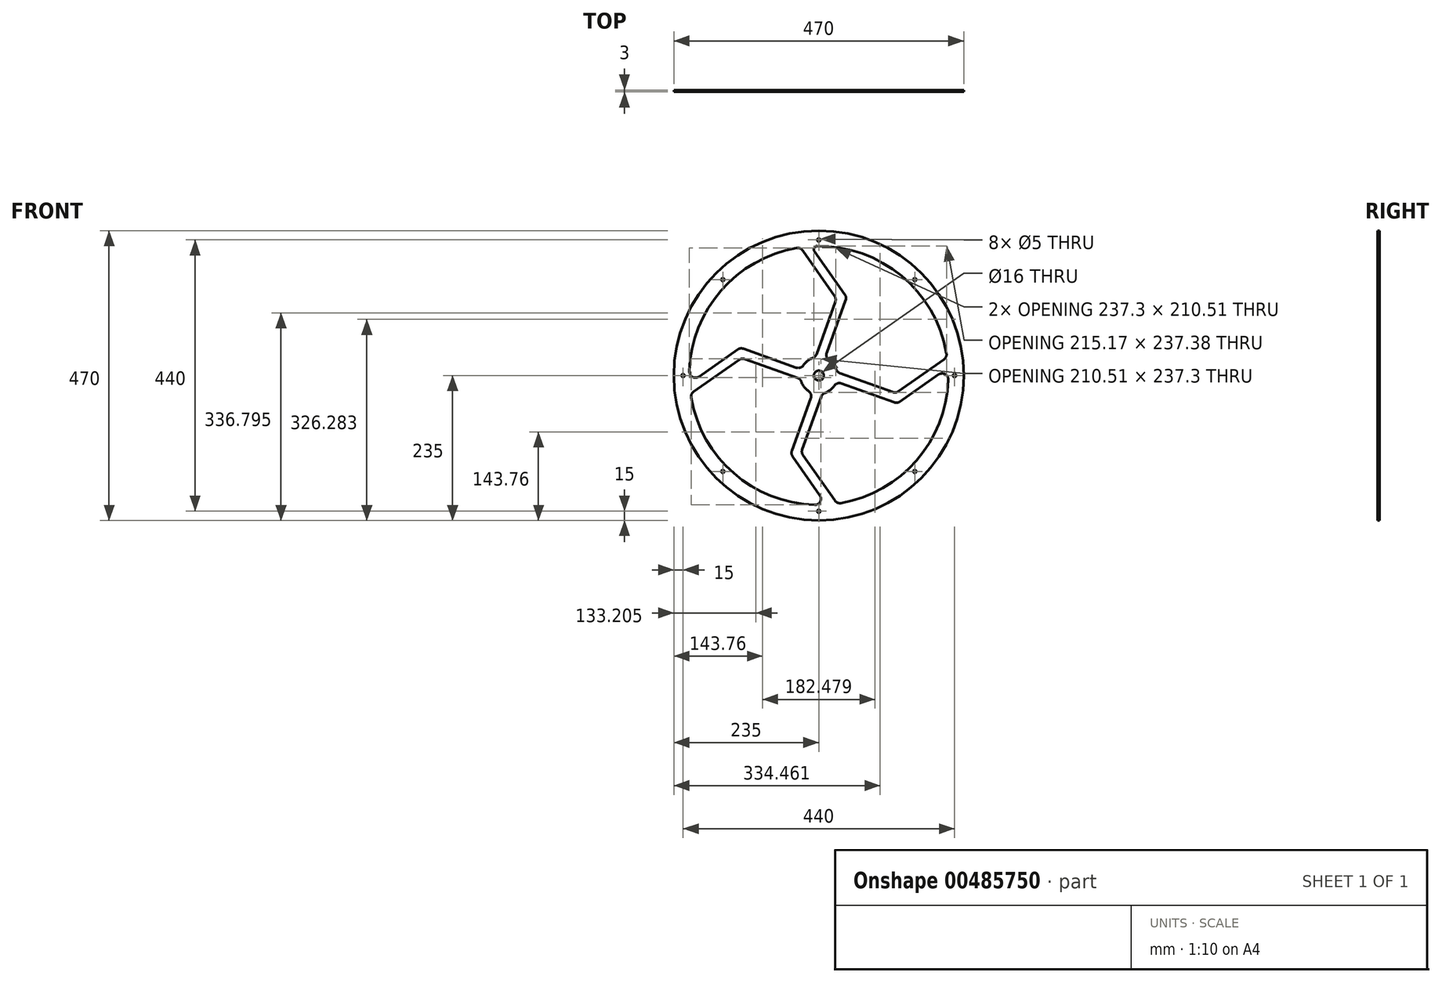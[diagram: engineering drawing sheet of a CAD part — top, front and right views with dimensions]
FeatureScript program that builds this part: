
annotation { "Feature Type Name" : "Feature", "Feature Type Description" : "" }
export const myFeature = defineFeature(function(context is Context, id is Id, definition is map)
    precondition{}
    {
        {
            var Q0;
            Q0=qCreatedBy(makeId("Front.planeOp"),FACE);
            var sketch = newSketch(context, id + "F0", { "sketchPlane" : qUnion([Q0]), "disableImprinting" : false});
            skCircle(sketch, "E0", {"center": v(0, 0) * mm, "radius": 235 * mm});
            skArc(sketch, "E1", {"start": v(206.9, 35.92) * mm, "mid": v(133.96, 161.72) * mm, "end": v(-3.21, 209.98) * mm});
            skArc(sketch, "E2", {"start": v(-9.97, 28.3) * mm, "mid": v(-18.38, 23.71) * mm, "end": v(-24.92, 16.7) * mm});
            skLineSegment(sketch, "E3", {"start": v(202.79, 26.02) * mm, "end": v(129.06, -25.6) * mm});
            skLineSegment(sketch, "E4", {"start": v(119.95, -26.82) * mm, "end": v(34.35, 3.87) * mm});
            skLineSegment(sketch, "E5", {"start": v(36.6, -12.87) * mm, "end": v(122.2, -43.56) * mm});
            skLineSegment(sketch, "E6", {"start": v(131.3, -42.34) * mm, "end": v(194.16, 1.67) * mm});
            skPoint(sketch, "E7.visualSharp", {"position": v(127.07, -45.31) * mm});
            skArc(sketch, "E7.filletArc", {"start": v(122.2, -43.56) * mm, "mid": v(126.9, -44.06) * mm, "end": v(131.3, -42.34) * mm});
            skPoint(sketch, "E8.visualSharp", {"position": v(124.82, -28.57) * mm});
            skArc(sketch, "E8.filletArc", {"start": v(119.95, -26.82) * mm, "mid": v(124.66, -27.32) * mm, "end": v(129.06, -25.6) * mm});
            skLineSegment(sketch, "E9.1.0", {"start": v(26.82, 119.95) * mm, "end": v(-3.87, 34.35) * mm});
            skArc(sketch, "E9.1.1", {"start": v(26.82, 119.95) * mm, "mid": v(27.32, 124.66) * mm, "end": v(25.6, 129.06) * mm});
            skLineSegment(sketch, "E9.1.2", {"start": v(-26.02, 202.79) * mm, "end": v(25.6, 129.06) * mm});
            skLineSegment(sketch, "E9.1.3", {"start": v(42.34, 131.3) * mm, "end": v(-7.23, 202.1) * mm});
            skArc(sketch, "E9.1.4", {"start": v(43.56, 122.2) * mm, "mid": v(44.06, 126.9) * mm, "end": v(42.34, 131.3) * mm});
            skLineSegment(sketch, "E9.1.5", {"start": v(12.87, 36.6) * mm, "end": v(43.56, 122.2) * mm});
            skLineSegment(sketch, "E9.2.0", {"start": v(-119.95, 26.82) * mm, "end": v(-34.35, -3.87) * mm});
            skArc(sketch, "E9.2.1", {"start": v(-119.95, 26.82) * mm, "mid": v(-124.66, 27.32) * mm, "end": v(-129.06, 25.6) * mm});
            skLineSegment(sketch, "E9.2.2", {"start": v(-202.79, -26.02) * mm, "end": v(-129.06, 25.6) * mm});
            skLineSegment(sketch, "E9.2.3", {"start": v(-131.3, 42.34) * mm, "end": v(-194.16, -1.67) * mm});
            skArc(sketch, "E9.2.4", {"start": v(-122.2, 43.56) * mm, "mid": v(-126.9, 44.06) * mm, "end": v(-131.3, 42.34) * mm});
            skLineSegment(sketch, "E9.2.5", {"start": v(-36.6, 12.87) * mm, "end": v(-122.2, 43.56) * mm});
            skLineSegment(sketch, "E10.2.3.0", {"start": v(-26.82, -119.95) * mm, "end": v(3.87, -34.35) * mm});
            skArc(sketch, "E10.3.3.0", {"start": v(-26.82, -119.95) * mm, "mid": v(-27.32, -124.66) * mm, "end": v(-25.6, -129.06) * mm});
            skLineSegment(sketch, "E10.7.3.0", {"start": v(26.02, -202.79) * mm, "end": v(-25.6, -129.06) * mm});
            skLineSegment(sketch, "E10.10.3.0", {"start": v(-42.34, -131.3) * mm, "end": v(1.67, -194.16) * mm});
            skArc(sketch, "E10.13.3.0", {"start": v(-43.56, -122.2) * mm, "mid": v(-44.06, -126.9) * mm, "end": v(-42.34, -131.3) * mm});
            skLineSegment(sketch, "E10.17.3.0", {"start": v(-12.87, -36.6) * mm, "end": v(-43.56, -122.2) * mm});
            skArc(sketch, "E11.trimOffspring", {"start": v(35.92, -206.9) * mm, "mid": v(158.46, -137.8) * mm, "end": v(209.89, -6.85) * mm});
            skArc(sketch, "E12.trimOffspring", {"start": v(-206.9, -35.92) * mm, "mid": v(-137.8, -158.46) * mm, "end": v(-6.85, -209.89) * mm});
            skArc(sketch, "E13.trimOffspring", {"start": v(-35.92, 206.9) * mm, "mid": v(-158.46, 137.8) * mm, "end": v(-209.89, 6.85) * mm});
            skPoint(sketch, "E14.visualSharp", {"position": v(209.63, 12.5) * mm});
            skArc(sketch, "E14.filletArc", {"start": v(209.89, -6.85) * mm, "mid": v(204.66, 2.27) * mm, "end": v(194.16, 1.67) * mm});
            skPoint(sketch, "E15.visualSharp", {"position": v(207.9, 29.6) * mm});
            skArc(sketch, "E15.filletArc", {"start": v(202.79, 26.02) * mm, "mid": v(206.29, 30.37) * mm, "end": v(206.9, 35.92) * mm});
            skPoint(sketch, "E16.visualSharp", {"position": v(-12.5, 209.63) * mm});
            skArc(sketch, "E16.filletArc", {"start": v(-3.21, 209.98) * mm, "mid": v(-7.59, 207.25) * mm, "end": v(-7.23, 202.1) * mm});
            skPoint(sketch, "E17.visualSharp", {"position": v(-29.6, 207.9) * mm});
            skArc(sketch, "E17.filletArc", {"start": v(-26.02, 202.79) * mm, "mid": v(-30.37, 206.29) * mm, "end": v(-35.92, 206.9) * mm});
            skPoint(sketch, "E18.visualSharp", {"position": v(-209.63, -12.5) * mm});
            skArc(sketch, "E18.filletArc", {"start": v(-209.89, 6.85) * mm, "mid": v(-204.66, -2.27) * mm, "end": v(-194.16, -1.67) * mm});
            skPoint(sketch, "E19.visualSharp", {"position": v(-207.9, -29.6) * mm});
            skArc(sketch, "E19.filletArc", {"start": v(-202.79, -26.02) * mm, "mid": v(-206.29, -30.37) * mm, "end": v(-206.9, -35.92) * mm});
            skPoint(sketch, "E20.visualSharp", {"position": v(12.5, -209.63) * mm});
            skArc(sketch, "E20.filletArc", {"start": v(-6.85, -209.89) * mm, "mid": v(2.27, -204.66) * mm, "end": v(1.67, -194.16) * mm});
            skPoint(sketch, "E21.visualSharp", {"position": v(29.6, -207.9) * mm});
            skArc(sketch, "E21.filletArc", {"start": v(26.02, -202.79) * mm, "mid": v(30.37, -206.29) * mm, "end": v(35.92, -206.9) * mm});
            skArc(sketch, "E22.trimOffspring", {"start": v(28.3, 9.97) * mm, "mid": v(23.71, 18.38) * mm, "end": v(16.7, 24.92) * mm});
            skArc(sketch, "E23.trimOffspring", {"start": v(-28.3, -9.97) * mm, "mid": v(-23.71, -18.38) * mm, "end": v(-16.7, -24.92) * mm});
            skArc(sketch, "E24.trimOffspring", {"start": v(9.97, -28.3) * mm, "mid": v(18.38, -23.71) * mm, "end": v(24.92, -16.7) * mm});
            skPoint(sketch, "E25.visualSharp", {"position": v(9.9, 28.32) * mm});
            skArc(sketch, "E25.filletArc", {"start": v(12.87, 36.6) * mm, "mid": v(12.78, 30.1) * mm, "end": v(16.7, 24.92) * mm});
            skPoint(sketch, "E26.visualSharp", {"position": v(29.47, 5.63) * mm});
            skArc(sketch, "E26.filletArc", {"start": v(28.3, 9.97) * mm, "mid": v(30.64, 6.24) * mm, "end": v(34.35, 3.87) * mm});
            skPoint(sketch, "E27.visualSharp", {"position": v(28.32, -9.9) * mm});
            skArc(sketch, "E27.filletArc", {"start": v(36.6, -12.87) * mm, "mid": v(30.1, -12.78) * mm, "end": v(24.92, -16.7) * mm});
            skPoint(sketch, "E28.visualSharp", {"position": v(5.63, -29.47) * mm});
            skArc(sketch, "E28.filletArc", {"start": v(9.97, -28.3) * mm, "mid": v(6.24, -30.64) * mm, "end": v(3.87, -34.35) * mm});
            skPoint(sketch, "E29.visualSharp", {"position": v(-9.9, -28.32) * mm});
            skArc(sketch, "E29.filletArc", {"start": v(-12.87, -36.6) * mm, "mid": v(-12.78, -30.1) * mm, "end": v(-16.7, -24.92) * mm});
            skPoint(sketch, "E30.visualSharp", {"position": v(-29.47, -5.63) * mm});
            skArc(sketch, "E30.filletArc", {"start": v(-28.3, -9.97) * mm, "mid": v(-30.64, -6.24) * mm, "end": v(-34.35, -3.87) * mm});
            skPoint(sketch, "E31.visualSharp", {"position": v(-28.32, 9.9) * mm});
            skArc(sketch, "E31.filletArc", {"start": v(-36.6, 12.87) * mm, "mid": v(-30.1, 12.78) * mm, "end": v(-24.92, 16.7) * mm});
            skPoint(sketch, "E32.visualSharp", {"position": v(-5.63, 29.47) * mm});
            skArc(sketch, "E32.filletArc", {"start": v(-9.97, 28.3) * mm, "mid": v(-6.24, 30.64) * mm, "end": v(-3.87, 34.35) * mm});
            skCircle(sketch, "E33", {"center": v(220, 0) * mm, "radius": 2.5 * mm});
            skCircle(sketch, "E34.1.0", {"center": v(0, 220) * mm, "radius": 2.5 * mm});
            skCircle(sketch, "E34.2.0", {"center": v(-220, 0) * mm, "radius": 2.5 * mm});
            skCircle(sketch, "E34.3.0", {"center": v(0, -220) * mm, "radius": 2.5 * mm});
            skCircle(sketch, "E35", {"center": v(0, 0) * mm, "radius": 8 * mm});
            skCircle(sketch, "E36", {"center": v(155.56, 155.56) * mm, "radius": 2.5 * mm});
            skLineSegment(sketch, "E37", {"start": v(0, 0) * mm, "end": v(155.56, 155.56) * mm, "construction": true});
            skCircle(sketch, "E38", {"center": v(0, 0) * mm, "radius": 220 * mm, "construction": true});
            skCircle(sketch, "E39.1.0", {"center": v(-155.56, 155.56) * mm, "radius": 2.5 * mm});
            skCircle(sketch, "E39.2.0", {"center": v(-155.56, -155.56) * mm, "radius": 2.5 * mm});
            skCircle(sketch, "E40.1.3.0", {"center": v(155.56, -155.56) * mm, "radius": 2.5 * mm});
            skSolve(sketch);
        }
        {
            var Q0;
            Q0 = qSketchRegion(id + "F0", true);
            extrude(context, id + "F1", {"entities" : qUnion([Q0]), "depth" : 3 * mm});
        }
    });
